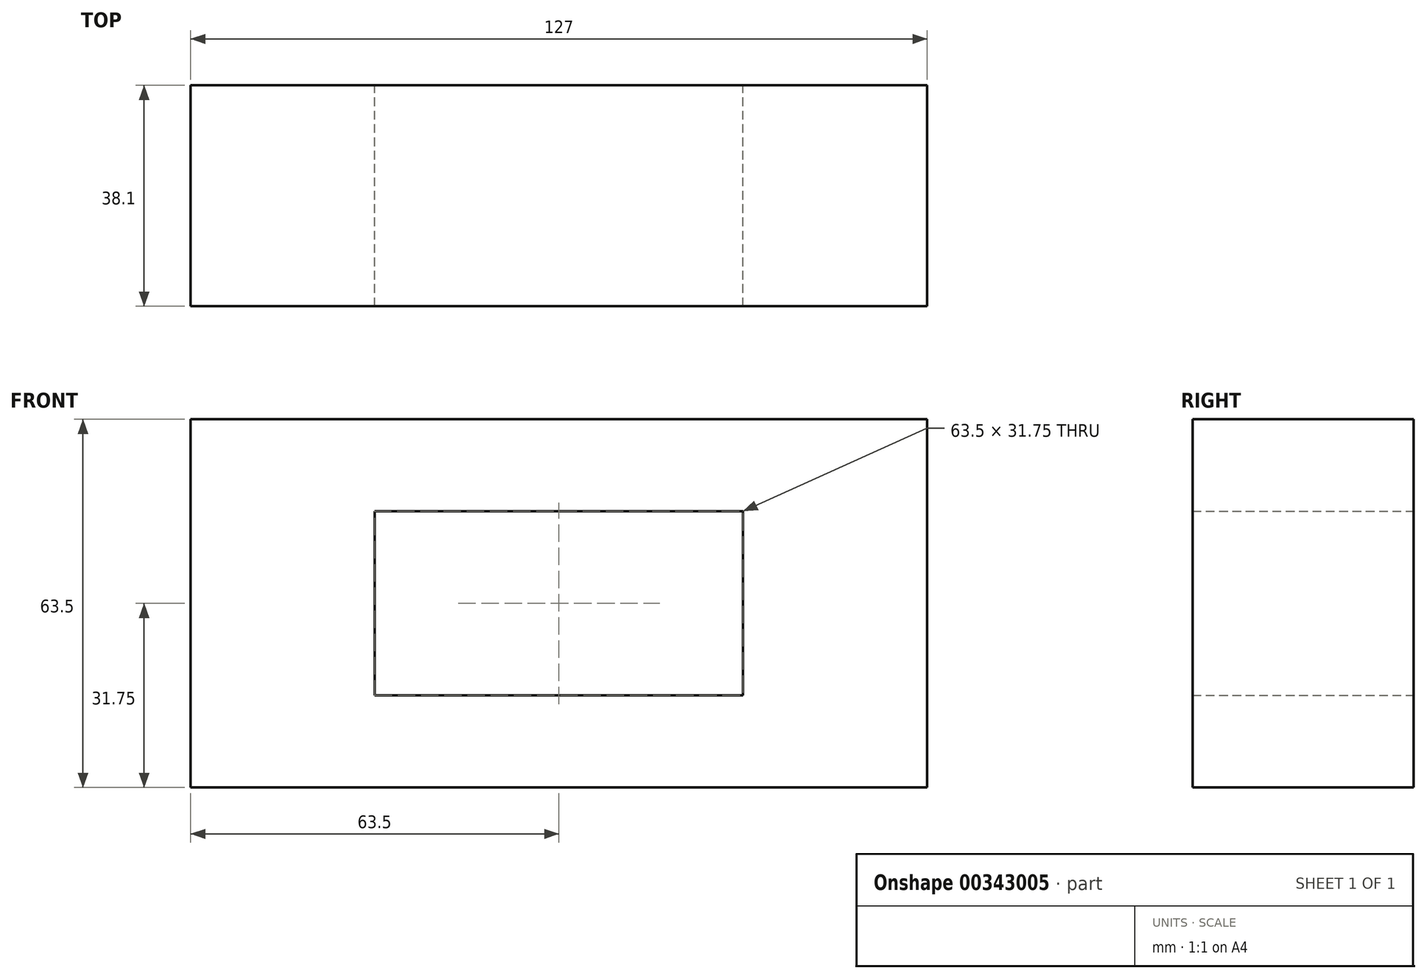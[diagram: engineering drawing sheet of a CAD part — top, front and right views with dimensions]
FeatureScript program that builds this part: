
annotation { "Feature Type Name" : "Feature", "Feature Type Description" : "" }
export const myFeature = defineFeature(function(context is Context, id is Id, definition is map)
    precondition{}
    {
        {
            var Q0;
            Q0=qCreatedBy(makeId("Front.planeOp"),FACE);
            var sketch = newSketch(context, id + "F0", { "sketchPlane" : qUnion([Q0])});
            skLineSegment(sketch, "E0.bottom", {"start": v(63.5, 31.75) * mm, "end": v(-63.5, 31.75) * mm});
            skLineSegment(sketch, "E0.top", {"start": v(63.5, -31.75) * mm, "end": v(-63.5, -31.75) * mm});
            skLineSegment(sketch, "E0.left", {"start": v(63.5, 31.75) * mm, "end": v(63.5, -31.75) * mm});
            skLineSegment(sketch, "E0.right", {"start": v(-63.5, 31.75) * mm, "end": v(-63.5, -31.75) * mm});
            skPoint(sketch, "E0.middle", {"position": v(0, 0) * mm});
            skLineSegment(sketch, "E1.bottom", {"start": v(31.75, 15.88) * mm, "end": v(-31.75, 15.88) * mm});
            skLineSegment(sketch, "E1.top", {"start": v(31.75, -15.88) * mm, "end": v(-31.75, -15.88) * mm});
            skLineSegment(sketch, "E1.left", {"start": v(31.75, 15.88) * mm, "end": v(31.75, -15.88) * mm});
            skLineSegment(sketch, "E1.right", {"start": v(-31.75, 15.88) * mm, "end": v(-31.75, -15.88) * mm});
            skSolve(sketch);
        }
        {
            var Q0;
            Q0=makeQuery(id+"F0.imprint","IMPRINT",FACE,{"disambiguationData":[TD([[makeQuery(id+"F0.imprint","IMPRINT",EDGE,{"derivedFrom":sQuery(id+"F0.wireOp",EDGE,"E0.bottom")}),1.0]])]});
            extrude(context, id + "F1", {"entities" : qUnion([Q0]), "depth" : 38.1 * mm});
        }
    });
